# Revit family: BE_84057_de_DE
name_source: partatom
category: Lighting Fixtures
units: mm (PartAtom-declared; Revit-internal decimal feet)

## family parameters
Cut with Voids When Loaded = Yes
Host = Face
Light Source = Yes
Part Type = Normal
Room Calculation Point = Yes
Round Connector Dimension = Use Diameter
Shared = No

## types (1)
- BEGA_84057_Grafit_K3
    AC/DC = AC/DC
    Aktualisierung = 2024-06-06T04:00:03
    Anschlussleitung = 5.0 m X05BQ-F 5 G 1 mm²
    Apparent Load = 0 VA
    BEGA_Dummy = No
    BEGA_IES = Yes
    BEGA_IES1 = Yes
    BEGA_IES2 = Yes
    BEGA_IES3 = Yes
    BEGA_Intern = Yes
    BEGA_Intern_Konstruktion = Yes
    BEGA_Intern_an = Yes
    BEGA_Intern_aus = Yes
    Beschreibung_Sonderanfertigung = Hier können Sie Informationen zur Sonderanfertigung eintragen.
    Bestellnummer = 84057K3
    CE_Konformität = ja
    Color Filter = 16777215
    Default Elevation = 0 mm  [stored 0 ft]
    Description = Aufsatzleuchte
    Dimming Lamp Color Temperature Shift = <None>
    ENEC = ja
    Einstecktiefe = 60 mm
    Energieeffizienzklasse = LED A++ - A
    Farbtemperatur = 3000 K
    Farbwiedergabeindex = CRI > 80
    Frequenz = 0/50-60 Hz
    Gewicht = 4.7 kg
    LED_Modulbezeichnung = LED-0770/830
    Lamp = LED 35.2 W
    Lampenlichtstrom = 6675 lm
    Lastklassifizierung = Beleuchtung
    Lebensdauerkriterien = L80B50 @ ta 25 °C = 200000 h
    Leuchtenlichtstrom = 4353 lm
    Logo = <None>
    M_A = No
    M_G = Yes
    M_W = No
    Manufacturer = BEGA
    Material_03 = BEGA_Oberfläche_Weiss_matt
    Material_04 = BEGA_Kunststoff_Grafit_matt
    Material_06 = BEGA_Oberfläche_Edelstahl_gebürstet
    Material_12 = BEGA_Kunststoff_klar
    Material_15 = BEGA_Leuchtmedium_matt
    Material_17 = BEGA_Reflektor
    Model = 84057K3
    Photometric Web File = BE_84057K3.IES
    Produktdatenblatt = https://cdn.bega.com
    Schutzart = IP 65
    Schutzklasse = I
    Sonderanfertigung = No
    Spannung = 240 V
    Tilt Angle = 0.00°
    URL = https://www.bega.com
    Umgebungstemperatur = 25 °C

note: [stored X ft] marks values corroborated as IEEE doubles in the binary element streams (Revit-internal decimal feet)
